# Revit family: Devens Chairs
name_source: partatom
category: Furniture
units: mm (PartAtom-declared; Revit-internal decimal feet)

## family parameters
Always vertical = Yes
Cut with Voids When Loaded = No
OmniClass Number = 23.40.20.00
OmniClass Title = General Furniture and Specialties
Room Calculation Point = No
Shared = No
Work Plane-Based = No

## types (4) — shared parameters
Manufacturer = AIS Inc
Product = DEVENS CHAIRS
URL = https://www.ais-inc.com
zero-valued in all types: Default Elevation

## per-type parameters (varying)
| type | Description | Model |
| 4600C-4D Arms | Configurable Mesh Task Chair with 4D Arms | 4600C |
| 4600C-No Arms | Configurable Mesh Task Chair with No Arms | 4600C |
| 4630C-4D Arms | Configurable Mesh Task Chair with 4D Arms | 4630C |
| 4630C-No Arms | Configurable Mesh Task Chair with No Arms | 4630C |

type visibility flags: 4 boolean params named "<type name>" — each type sets only its own to Yes (folded from table)

## geometry (parser evidence)
native form markers: Sweep x3
no freeform markers — native parametric forms only
